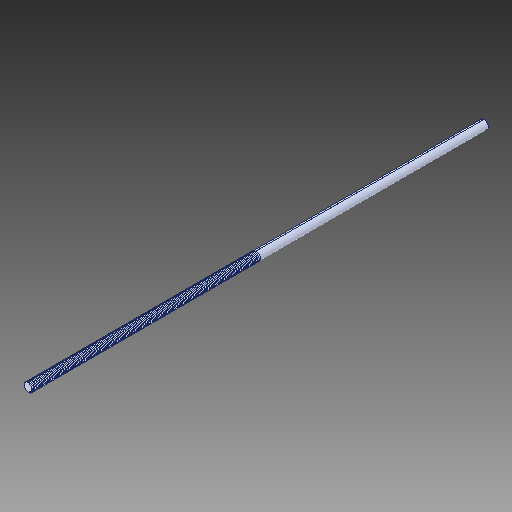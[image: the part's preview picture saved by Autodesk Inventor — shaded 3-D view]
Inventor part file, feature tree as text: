
AUTODESK INVENTOR PART (.ipt)
format: ipt  version: 2019 (Build 230136000, 136)  size: 2,268,672 bytes
history: native  units: in
note: dims shown in document units (in); Inventor stores cm internally (conversion verified against a paired STEP export)
features: other x2, projected_geometry x2, extrude x1, sketch x1
ambient origin geometry x8: Origin, YZ Plane, XZ Plane, XY Plane, X Axis, Y Axis, Z Axis, Center Point
bodies: Solid1 (feature_tree)
feature tree (6):
  other  "LeadScrew 8mm x 2mmPitch.STEP"
  extrude  "Extrusion1"  [1 undecoded]
  sketch  "Sketch1"  dims[d0=7.874in d1=0.0in]
  projected_geometry  "Projected Loop1"
  projected_geometry  "Projected Loop2"
  other  "Cut-Sweep1"
note: 1 required parameter value undecoded (feature->parameter linkage not recoverable at this tier; creation-order binding heuristic only, values carry confidence <= 0.55)
